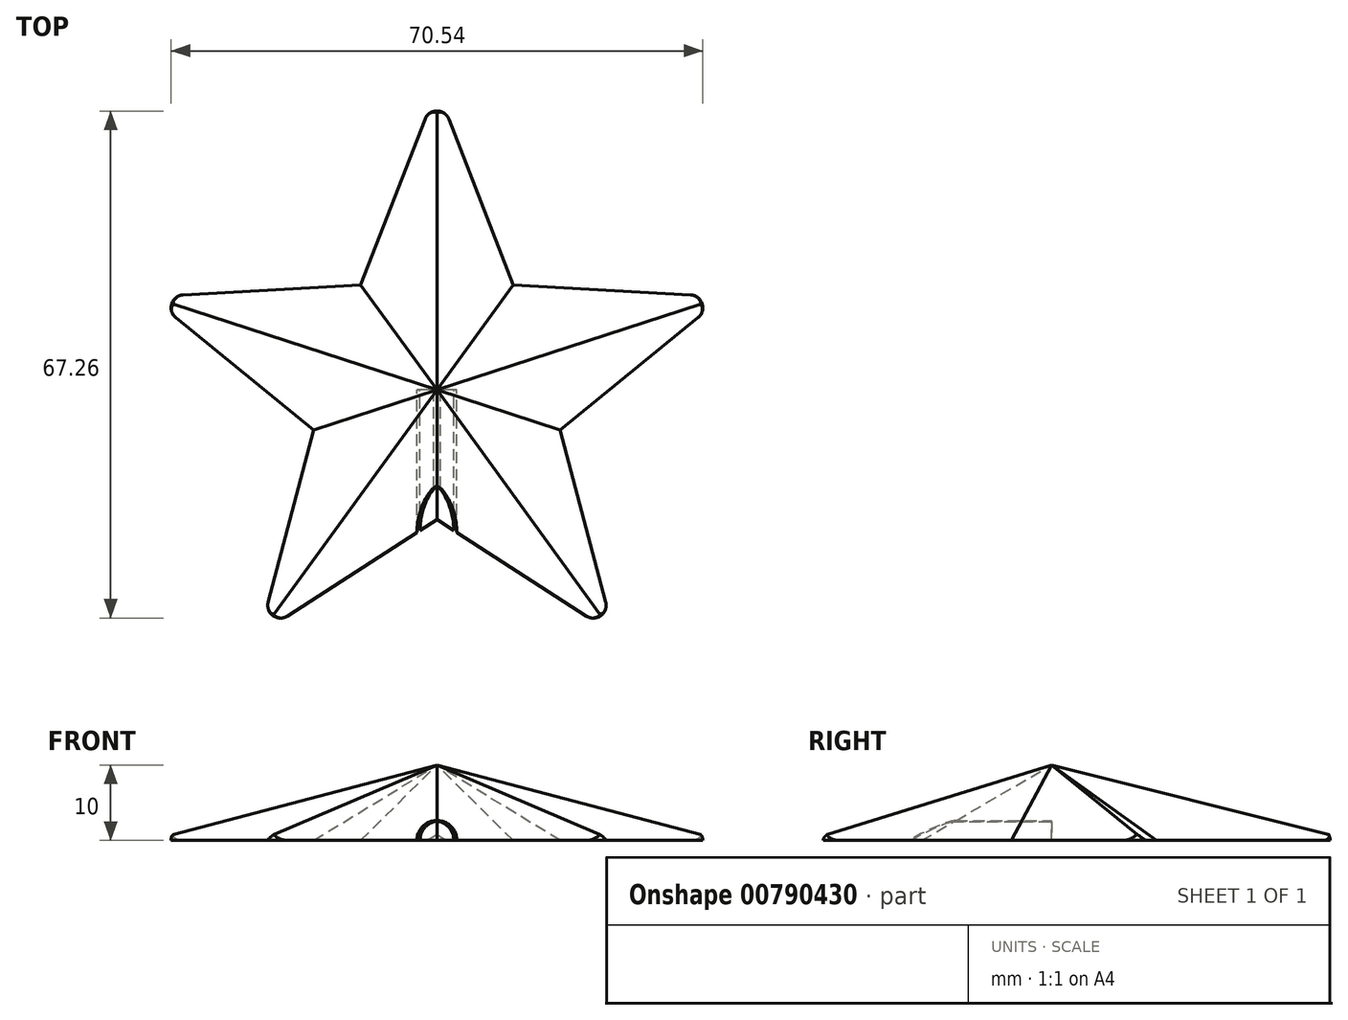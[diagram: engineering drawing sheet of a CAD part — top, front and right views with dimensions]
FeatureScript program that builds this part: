
annotation { "Feature Type Name" : "Feature", "Feature Type Description" : "" }
export const myFeature = defineFeature(function(context is Context, id is Id, definition is map)
    precondition{}
    {
        {
            assignVariable(context, id + "F0", {"name" : "hdist", "anyValue" : 0.4});
        }
        {
            var Q0;
            Q0=qCreatedBy(makeId("Top.planeOp"),FACE);
            var sketch = newSketch(context, id + "F1", { "sketchPlane" : qUnion([Q0])});
            skCircle(sketch, "E0.cCircle", {"center": v(0, 0) * mm, "radius": 32.36 * mm, "construction": true});
            skLineSegment(sketch, "E0.0", {"start": v(0, 40) * mm, "end": v(38.04, 12.36) * mm, "construction": true});
            skLineSegment(sketch, "E0.1", {"start": v(38.04, 12.36) * mm, "end": v(23.51, -32.36) * mm, "construction": true});
            skLineSegment(sketch, "E0.2", {"start": v(23.51, -32.36) * mm, "end": v(-23.51, -32.36) * mm, "construction": true});
            skLineSegment(sketch, "E0.3", {"start": v(-23.51, -32.36) * mm, "end": v(-38.04, 12.36) * mm, "construction": true});
            skLineSegment(sketch, "E0.4", {"start": v(-38.04, 12.36) * mm, "end": v(0, 40) * mm, "construction": true});
            skPoint(sketch, "E0.0.midPoint", {"position": v(19.02, 26.18) * mm});
            skCircle(sketch, "E1.cCircle", {"center": v(0, 0) * mm, "radius": 13.92 * mm, "construction": true});
            skLineSegment(sketch, "E1.0", {"start": v(-10.1, 13.92) * mm, "end": v(10.1, 13.92) * mm, "construction": true});
            skLineSegment(sketch, "E1.1", {"start": v(10.1, 13.92) * mm, "end": v(16.36, -5.32) * mm, "construction": true});
            skLineSegment(sketch, "E1.2", {"start": v(16.36, -5.32) * mm, "end": v(0, -17.2) * mm, "construction": true});
            skLineSegment(sketch, "E1.3", {"start": v(0, -17.2) * mm, "end": v(-16.36, -5.32) * mm, "construction": true});
            skLineSegment(sketch, "E1.4", {"start": v(-16.36, -5.32) * mm, "end": v(-10.1, 13.92) * mm, "construction": true});
            skPoint(sketch, "E1.0.midPoint", {"position": v(0, 13.92) * mm});
            skLineSegment(sketch, "E2", {"start": v(0, 40) * mm, "end": v(10.1, 13.92) * mm});
            skLineSegment(sketch, "E3", {"start": v(0, 40) * mm, "end": v(-10.1, 13.92) * mm});
            skLineSegment(sketch, "E4", {"start": v(16.36, -5.32) * mm, "end": v(38.04, 12.36) * mm});
            skLineSegment(sketch, "E5", {"start": v(-10.1, 13.92) * mm, "end": v(0, 0) * mm});
            skLineSegment(sketch, "E6", {"start": v(10.1, 13.92) * mm, "end": v(0, 0) * mm});
            skSolve(sketch);
        }
        {
            var Q0;
            Q0=qCreatedBy(makeId("Right.planeOp"),FACE);
            var sketch = newSketch(context, id + "F2", { "sketchPlane" : qUnion([Q0])});
            skLineSegment(sketch, "E7", {"start": v(0, 0) * mm, "end": v(0, 10) * mm, "construction": true});
            skSolve(sketch);
        }
        {
            var Q0;
            Q0=makeQuery(id+"F1.imprint","IMPRINT",FACE,{"disambiguationData":[TD([[makeQuery(id+"F1.imprint","IMPRINT",EDGE,{"derivedFrom":sQuery(id+"F1.wireOp",EDGE,"E2")}),-1.0]])]});
            var Q1;
            Q1=sQuery(id+"F2.wireOp",VERTEX,"E7.end");
            loft(context, id + "F3", {"sheetProfilesArray" : [{ "sheetProfileEntities" : qUnion([Q0]) }, { "sheetProfileEntities" : qUnion([Q1]) }]});
        }
        {
            var Q0;
            Q0=qCreatedBy(makeId("Top.planeOp"),FACE);
            var sketch = newSketch(context, id + "F4", { "sketchPlane" : qUnion([Q0])});
            skArc(sketch, "E8", {"start": v(-1.58, 35.92) * mm, "mid": v(0, 37) * mm, "end": v(1.58, 35.92) * mm});
            skLineSegment(sketch, "E9", {"start": v(-7.83, 35.3) * mm, "end": v(10.46, 35.3) * mm, "construction": true});
            skLineSegment(sketch, "E10", {"start": v(-1.58, 35.92) * mm, "end": v(-1.58, 35.3) * mm});
            skLineSegment(sketch, "E11", {"start": v(1.58, 35.92) * mm, "end": v(1.58, 35.3) * mm});
            skLineSegment(sketch, "E12", {"start": v(-1.58, 35.3) * mm, "end": v(1.58, 35.3) * mm});
            skSolve(sketch);
        }
        {
            var Q0;
            Q0 = qSketchRegion(id + "F4", true);
            var Q1;
            Q1=sQuery(id+"F4.wireOp",EDGE,"E12");
            revolve(context, id + "F5", {"surfaceOperationType" : NewSurfaceOperationType.NEW, "entities" : qUnion([Q0]), "axis" : qUnion([Q1]), "revolveType" : RevolveType.SYMMETRIC, "angle" : 180 * degree});
        }
        {
            var Q0;
            Q0=makeQuery(id+"F5.opRevolve","CAP_FACE",FACE,{"disambiguationData":[OSD([sQuery(id+"F4.wireOp",EDGE,"E8"),sQuery(id+"F4.wireOp",EDGE,"E10"),sQuery(id+"F4.wireOp",EDGE,"E11"),sQuery(id+"F4.wireOp",EDGE,"E12")])],"isStart":true});
            var Q1;
            Q1=makeQuery(id+"F3.opLoft","MID_CAP_VERTEX",VERTEX,{"disambiguationData":[OSD([sQuery(id+"F1.wireOp",EDGE,"E2"),sQuery(id+"F1.wireOp",EDGE,"E3")])],"capPos":0.0});
            extrude(context, id + "F6", {"entities" : qUnion([Q0]), "endBound" : BoundingType.UP_TO_VERTEX, "oppositeDirection" : true, "depth" : 5 * mm, "endBoundEntityVertex" : qUnion([Q1]), "offsetDistance" : 25 * mm});
        }
        {
            var Q0;
            Q0=makeQuery(id+"F5.opRevolve","SWEPT_BODY",BODY,{"disambiguationData":[OSD([sQuery(id+"F4.wireOp",EDGE,"E8"),sQuery(id+"F4.wireOp",EDGE,"E10"),sQuery(id+"F4.wireOp",EDGE,"E11"),sQuery(id+"F4.wireOp",EDGE,"E12")])]});
            var Q1;
            Q1=makeQuery(id+"F6.opExtrude","SWEPT_BODY",BODY,{"disambiguationData":[OSD([sQuery(id+"F4.wireOp",EDGE,"E8"),sQuery(id+"F4.wireOp",EDGE,"E10"),sQuery(id+"F4.wireOp",EDGE,"E11"),sQuery(id+"F4.wireOp",EDGE,"E12")])]});
            booleanBodies(context, id + "F7", {"operationType" : BooleanOperationType.SUBTRACTION, "tools" : qUnion([Q0]), "targets" : qUnion([Q1])});
        }
        {
            var Q0;
            Q0=makeQuery(id+"F6.opExtrude","SWEPT_BODY",BODY,{"disambiguationData":[OSD([sQuery(id+"F4.wireOp",EDGE,"E8"),sQuery(id+"F4.wireOp",EDGE,"E10"),sQuery(id+"F4.wireOp",EDGE,"E11"),sQuery(id+"F4.wireOp",EDGE,"E12")])]});
            var Q1;
            Q1=makeQuery(id+"F3.opLoft","SWEPT_BODY",BODY,{"disambiguationData":[OSD([makeQuery(id+"F1.imprint","IMPRINT",FACE,{"disambiguationData":[TD([[makeQuery(id+"F1.imprint","IMPRINT",EDGE,{"derivedFrom":sQuery(id+"F1.wireOp",EDGE,"E2")}),-1.0]])]}),sQuery(id+"F2.wireOp",VERTEX,"E7.end")])]});
            booleanBodies(context, id + "F8", {"operationType" : BooleanOperationType.SUBTRACTION, "tools" : qUnion([Q0]), "targets" : qUnion([Q1])});
        }
        {
            var Q0;
            Q0=makeQuery(id+"F3.opLoft","SWEPT_BODY",BODY,{"disambiguationData":[OSD([makeQuery(id+"F1.imprint","IMPRINT",FACE,{"disambiguationData":[TD([[makeQuery(id+"F1.imprint","IMPRINT",EDGE,{"derivedFrom":sQuery(id+"F1.wireOp",EDGE,"E2")}),-1.0]])]}),sQuery(id+"F2.wireOp",VERTEX,"E7.end")])]});
            var Q1;
            Q1=makeQuery(id+"F3.opLoft","SWEPT_EDGE",EDGE,{"disambiguationData":[OSD([sQuery(id+"F1.wireOp",EDGE,"E5"),sQuery(id+"F1.wireOp",EDGE,"E6"),sQuery(id+"F2.wireOp",VERTEX,"E7.end")])]});
            circularPattern(context, id + "F9", {"operationType" : NewBodyOperationType.ADD, "entities" : qUnion([Q0]), "axis" : qUnion([Q1]), "angle" : 360 * degree, "instanceCount" : 5, "equalSpace" : true});
        }
        {
            var Q0;
            Q0=qCreatedBy(makeId("Front.planeOp"),FACE);
            var sketch = newSketch(context, id + "F10", { "sketchPlane" : qUnion([Q0])});
            skCircle(sketch, "E13", {"center": v(0, 0) * mm, "radius": 2.65 * mm});
            skArc(sketch, "E14", {"start": v(-2.25, 0) * mm, "mid": v(-1.75, 1.55) * mm, "end": v(-0.44, 2.51) * mm});
            skArc(sketch, "E15.MirrorCS", {"start": v(2.25, 0) * mm, "mid": v(1.75, 1.55) * mm, "end": v(0.44, 2.51) * mm});
            skLineSegment(sketch, "E16", {"start": v(-2.25, 0) * mm, "end": v(2.25, 0) * mm});
            skArc(sketch, "E17", {"start": v(-0.44, 2.51) * mm, "mid": v(0, 2.55) * mm, "end": v(0.44, 2.51) * mm});
            skSolve(sketch);
        }
        {
            var Q0;
            Q0=makeQuery(id+"F10.imprint","IMPRINT",FACE,{"disambiguationData":[TD([[makeQuery(id+"F10.imprint","IMPRINT",EDGE,{"derivedFrom":sQuery(id+"F10.wireOp",EDGE,"E14")}),-1.0]])]});
            extrude(context, id + "F11", {"entities" : qUnion([Q0]), "operationType" : NewBodyOperationType.REMOVE, "depth" : (getVariable(context, 'hdist')) * mm, "offsetDistance" : 25 * mm});
        }
        {
            var Q0;
            Q0=makeQuery(id+"F10.imprint","IMPRINT",FACE,{"disambiguationData":[TD([[makeQuery(id+"F10.imprint","IMPRINT",EDGE,{"derivedFrom":sQuery(id+"F10.wireOp",EDGE,"E13")}),1.0]])]});
            extrude(context, id + "F12", {"entities" : qUnion([Q0]), "operationType" : NewBodyOperationType.REMOVE, "endBound" : BoundingType.THROUGH_ALL, "depth" : 25 * mm, "offsetDistance" : 25 * mm});
        }
    });
